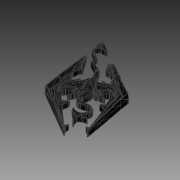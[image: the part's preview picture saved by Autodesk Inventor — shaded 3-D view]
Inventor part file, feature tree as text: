
AUTODESK INVENTOR PART (.ipt)
format: ipt  version: 2018 (Build 220112000, 112)  size: 3,113,472 bytes
history: native  units: mm
features: other x4, extrude x1, sketch x1
ambient origin geometry x8: Origin, YZ Plane, XZ Plane, XY Plane, X Axis, Y Axis, Z Axis, Center Point
bodies: Body1 (feature_tree)
feature tree (6):
  other  "skyrimlogo2.ipt"
  extrude  "押し出し1"  Depth=0.769231mm
  other  "ソリッド1::skyrimlogo2.ipt"
  other  "TaggingFeature1"
  sketch  "スケッチ1"
  other  "ソリッド1"
